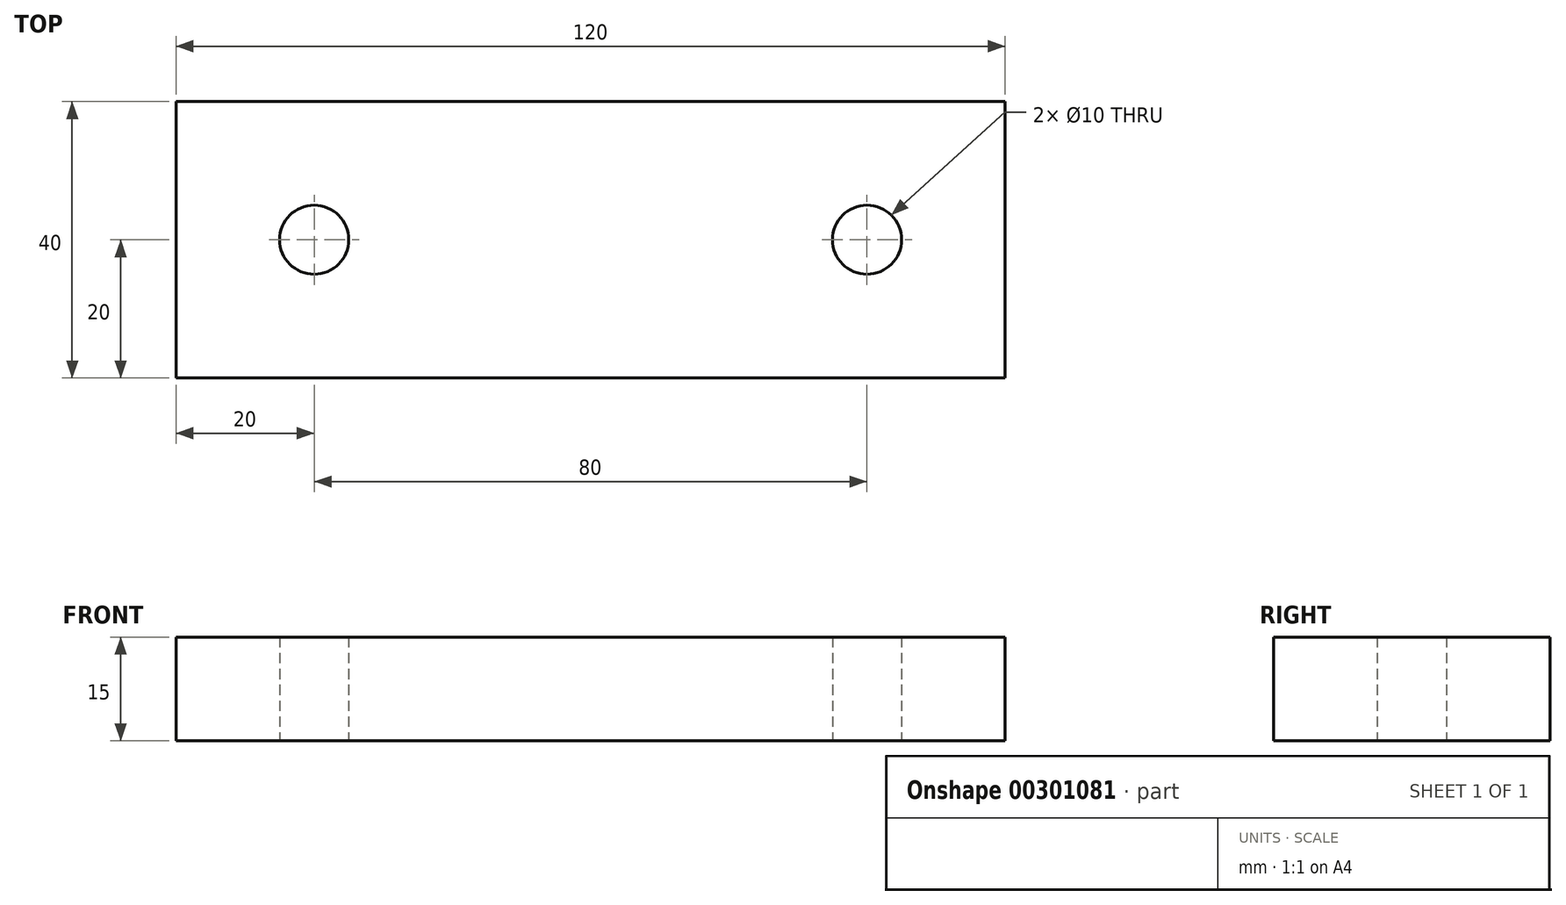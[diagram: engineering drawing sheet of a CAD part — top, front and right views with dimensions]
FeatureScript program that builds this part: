
annotation { "Feature Type Name" : "Feature", "Feature Type Description" : "" }
export const myFeature = defineFeature(function(context is Context, id is Id, definition is map)
    precondition{}
    {
        {
            var Q0;
            Q0=qCreatedBy(makeId("Top.planeOp"),FACE);
            var sketch = newSketch(context, id + "F0", { "sketchPlane" : qUnion([Q0])});
            skLineSegment(sketch, "E0", {"start": v(-60, 0) * mm, "end": v(60, 0) * mm});
            skLineSegment(sketch, "E1", {"start": v(60, 0) * mm, "end": v(60, -40) * mm});
            skLineSegment(sketch, "E2", {"start": v(60, -40) * mm, "end": v(-60, -40) * mm});
            skLineSegment(sketch, "E3", {"start": v(-60, -40) * mm, "end": v(-60, 0) * mm});
            skCircle(sketch, "E4", {"center": v(-40, -20) * mm, "radius": 5 * mm});
            skCircle(sketch, "E5", {"center": v(40, -20) * mm, "radius": 5 * mm});
            skSolve(sketch);
        }
        {
            var Q0;
            Q0=makeQuery(id+"F0.imprint","IMPRINT",FACE,{"disambiguationData":[TD([[makeQuery(id+"F0.imprint","IMPRINT",EDGE,{"derivedFrom":sQuery(id+"F0.wireOp",EDGE,"E0")}),-1.0]])]});
            extrude(context, id + "F1", {"entities" : qUnion([Q0]), "depth" : 15 * mm});
        }
    });
